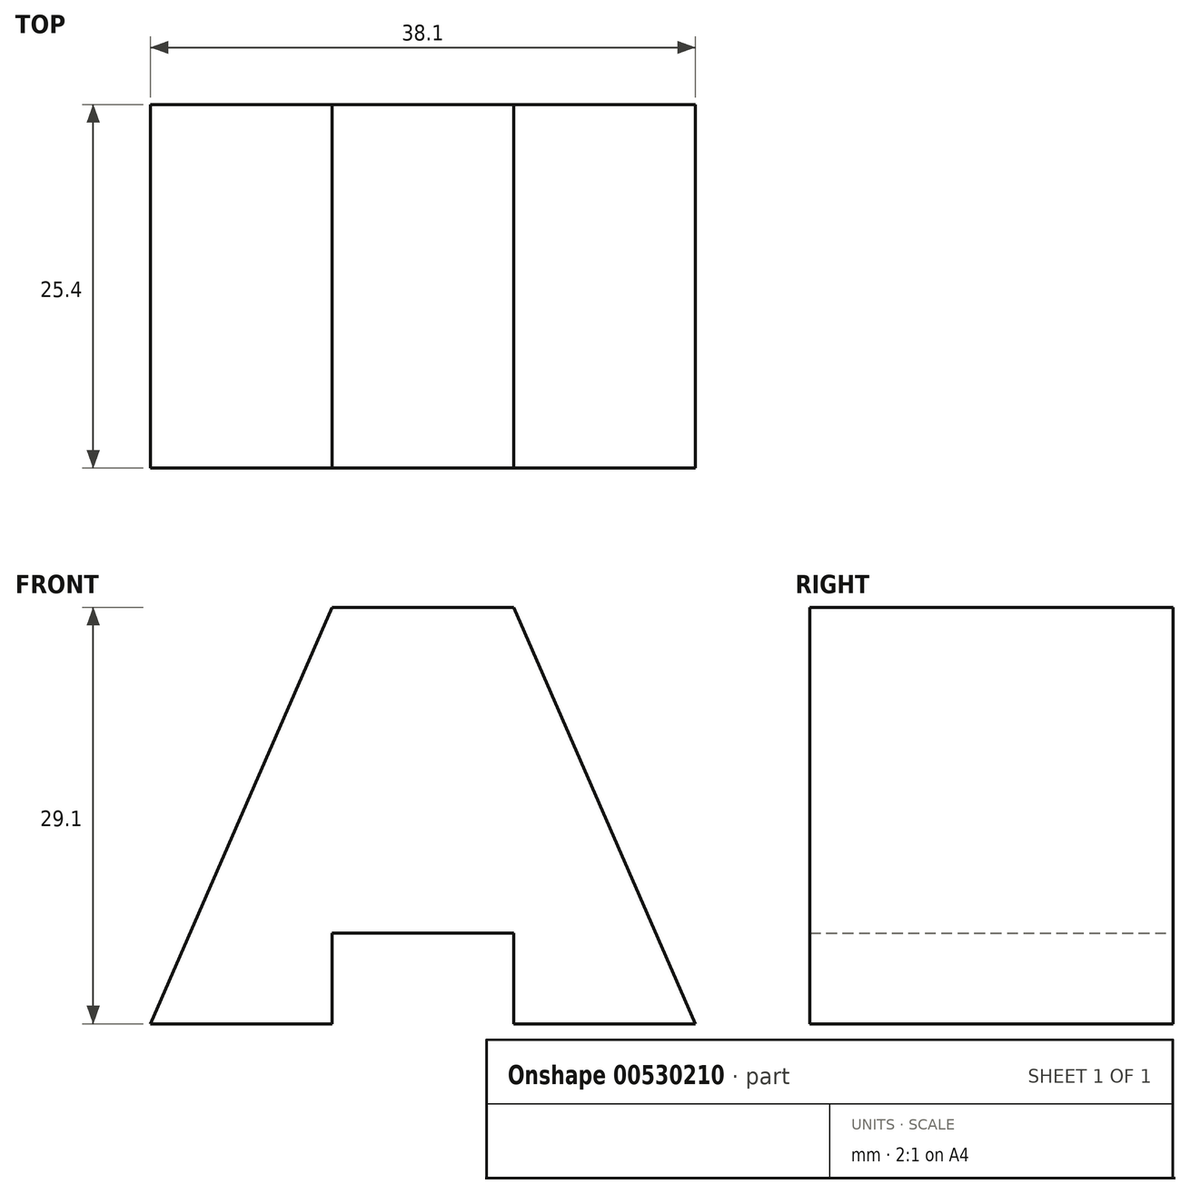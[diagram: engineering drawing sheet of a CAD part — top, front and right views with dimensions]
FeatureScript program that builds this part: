
annotation { "Feature Type Name" : "Feature", "Feature Type Description" : "" }
export const myFeature = defineFeature(function(context is Context, id is Id, definition is map)
    precondition{}
    {
        {
            var Q0;
            Q0=qCreatedBy(makeId("Front.planeOp"),FACE);
            var sketch = newSketch(context, id + "F0", { "sketchPlane" : qUnion([Q0])});
            skLineSegment(sketch, "E0", {"start": v(-65.01, 0) * mm, "end": v(-52.31, 0) * mm});
            skLineSegment(sketch, "E1", {"start": v(-52.31, 0) * mm, "end": v(-52.31, 6.35) * mm});
            skLineSegment(sketch, "E2", {"start": v(-52.31, 6.35) * mm, "end": v(-39.61, 6.35) * mm});
            skLineSegment(sketch, "E3", {"start": v(-39.61, 6.35) * mm, "end": v(-39.61, 0) * mm});
            skLineSegment(sketch, "E4", {"start": v(-39.61, 0) * mm, "end": v(-26.91, 0) * mm});
            skLineSegment(sketch, "E5", {"start": v(-26.91, 0) * mm, "end": v(-39.61, 29.1) * mm});
            skLineSegment(sketch, "E6", {"start": v(-39.61, 29.1) * mm, "end": v(-52.31, 29.1) * mm});
            skLineSegment(sketch, "E7", {"start": v(-52.31, 29.1) * mm, "end": v(-65.01, 0) * mm});
            skSolve(sketch);
        }
        {
            var Q0;
            Q0=makeQuery(id+"F0.imprint","IMPRINT",FACE,{"disambiguationData":[TD([[makeQuery(id+"F0.imprint","IMPRINT",EDGE,{"derivedFrom":sQuery(id+"F0.wireOp",EDGE,"E0")}),1.0]])]});
            extrude(context, id + "F1", {"entities" : qUnion([Q0]), "depth" : 25.4 * mm, "offsetDistance" : 25.4 * mm});
        }
    });
